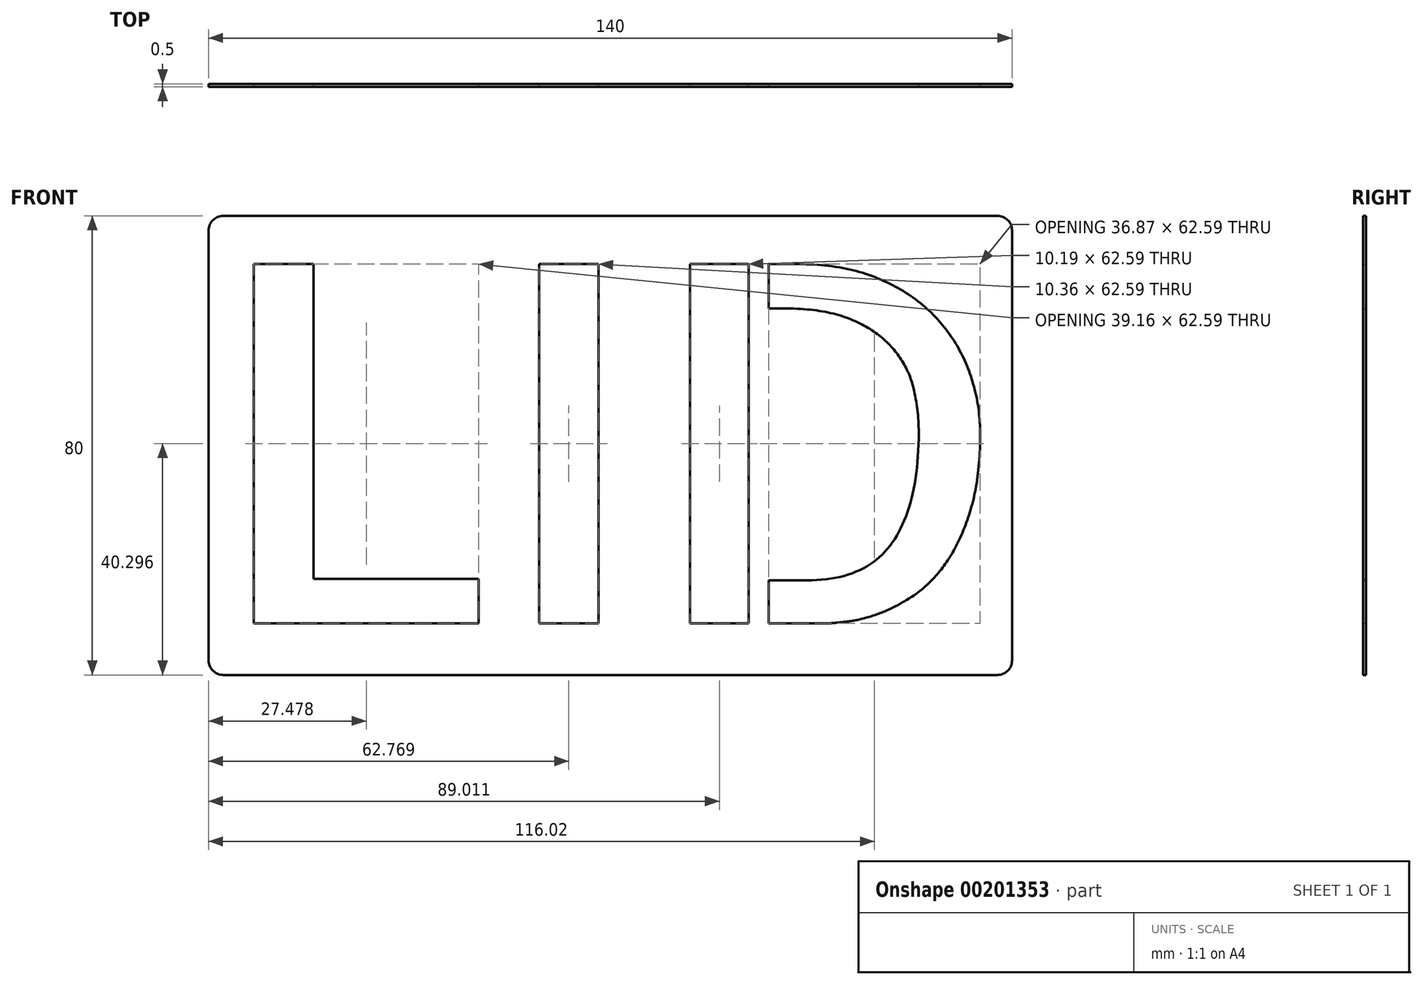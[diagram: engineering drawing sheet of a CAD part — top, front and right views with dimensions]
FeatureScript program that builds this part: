
annotation { "Feature Type Name" : "Feature", "Feature Type Description" : "" }
export const myFeature = defineFeature(function(context is Context, id is Id, definition is map)
    precondition{}
    {
        {
            var Q0;
            Q0=qCreatedBy(makeId("Front.planeOp"),FACE);
            var sketch = newSketch(context, id + "F0", { "sketchPlane" : qUnion([Q0])});
            skText(sketch, "E0", { "text": "LID \n", "fontName": "AllertaStencil-Regular.ttf"});
            skLineSegment(sketch, "E1.bottom", {"start": v(0, 32.7) * mm, "end": v(134.92, 32.7) * mm});
            skLineSegment(sketch, "E1.top", {"start": v(0, -47.3) * mm, "end": v(134.92, -47.3) * mm});
            skLineSegment(sketch, "E1.left", {"start": v(-2.54, 30.16) * mm, "end": v(-2.54, -44.76) * mm});
            skLineSegment(sketch, "E1.right", {"start": v(137.46, 30.16) * mm, "end": v(137.46, -44.76) * mm});
            skPoint(sketch, "E2.visualSharp", {"position": v(-2.54, 32.7) * mm});
            skArc(sketch, "E2.filletArc", {"start": v(0, 32.7) * mm, "mid": v(-1.8, 31.96) * mm, "end": v(-2.54, 30.16) * mm});
            skPoint(sketch, "E3.visualSharp", {"position": v(137.46, 32.7) * mm});
            skArc(sketch, "E3.filletArc", {"start": v(137.46, 30.16) * mm, "mid": v(136.72, 31.96) * mm, "end": v(134.92, 32.7) * mm});
            skPoint(sketch, "E4.visualSharp", {"position": v(137.46, -47.3) * mm});
            skArc(sketch, "E4.filletArc", {"start": v(134.92, -47.3) * mm, "mid": v(136.72, -46.55) * mm, "end": v(137.46, -44.76) * mm});
            skPoint(sketch, "E5.visualSharp", {"position": v(-2.54, -47.3) * mm});
            skArc(sketch, "E5.filletArc", {"start": v(-2.54, -44.76) * mm, "mid": v(-1.8, -46.55) * mm, "end": v(0, -47.3) * mm});
            const initialGuessF0  = {"E0": [-0.00254, -0.0383, 1, 0, 0.06262]};
            skSetInitialGuess(sketch, initialGuessF0);
            skSolve(sketch);
        }
        {
            var Q0;
            Q0=makeQuery(id+"F0.imprint","IMPRINT",FACE,{"disambiguationData":[TD([[makeQuery(id+"F0.imprint","IMPRINT",EDGE,{"derivedFrom":sQuery(id+"F0.wireOp",EDGE,"E0.sketch_text.stroke-0")}),1.0]])]});
            extrude(context, id + "F1", {"entities" : qUnion([Q0]), "depth" : 0.5 * mm});
        }
    });
